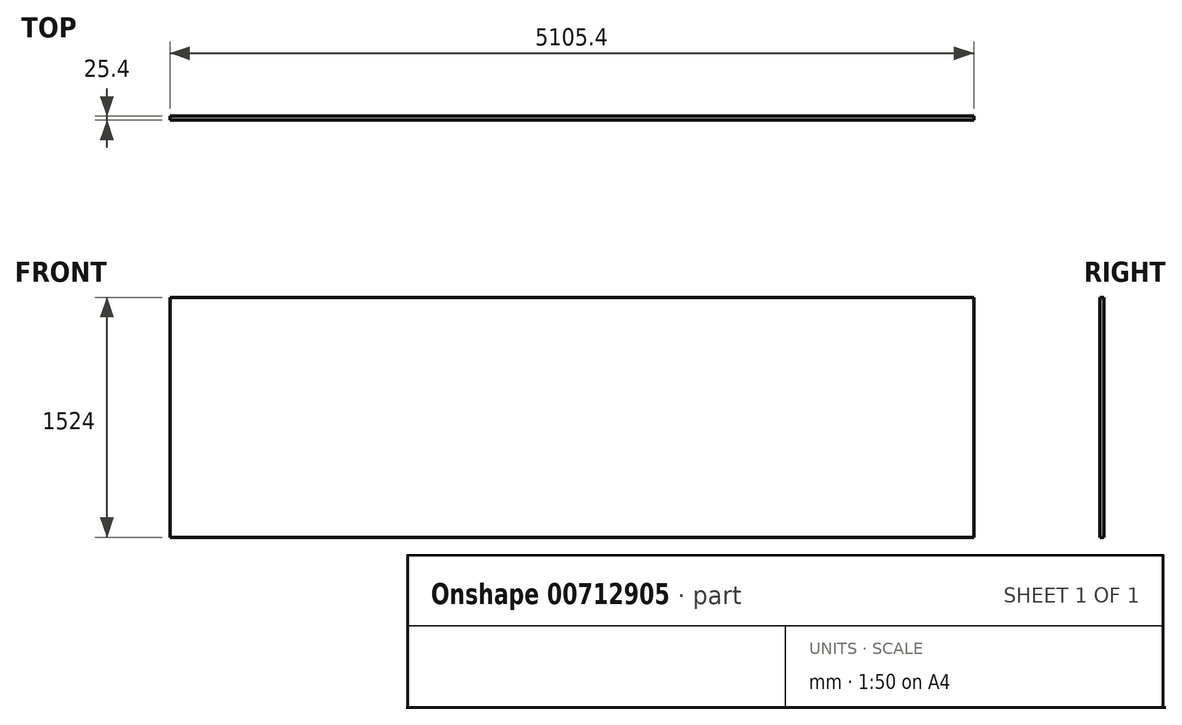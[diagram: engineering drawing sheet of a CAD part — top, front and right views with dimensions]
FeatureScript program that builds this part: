
annotation { "Feature Type Name" : "Feature", "Feature Type Description" : "" }
export const myFeature = defineFeature(function(context is Context, id is Id, definition is map)
    precondition{}
    {
        {
            var Q0;
            Q0=qCreatedBy(makeId("Front.planeOp"),FACE);
            var sketch = newSketch(context, id + "F0", { "sketchPlane" : qUnion([Q0])});
            skLineSegment(sketch, "E0.bottom", {"start": v(-2437.72, 1524) * mm, "end": v(2642.28, 1524) * mm});
            skLineSegment(sketch, "E0.top", {"start": v(-2437.72, 0) * mm, "end": v(2642.28, 0) * mm});
            skLineSegment(sketch, "E0.left", {"start": v(-2437.72, 1524) * mm, "end": v(-2437.72, 0) * mm});
            skLineSegment(sketch, "E0.right", {"start": v(2642.28, 1524) * mm, "end": v(2642.28, 0) * mm});
            skSolve(sketch);
        }
        {
            var Q0;
            Q0 = qSketchRegion(id + "F0", true);
            extrude(context, id + "F1", {"entities" : qUnion([Q0]), "oppositeDirection" : true, "depth" : 25.4 * mm, "offsetDistance" : 25.4 * mm});
        }
        {
            var Q0;
            Q0=makeQuery(id+"F1.opExtrude","SWEPT_FACE",FACE,{"disambiguationData":[OSD([sQuery(id+"F0.wireOp",EDGE,"E0.right")])]});
            extrude(context, id + "F2", {"entities" : qUnion([Q0]), "operationType" : NewBodyOperationType.ADD, "depth" : 25.4 * mm, "offsetDistance" : 25.4 * mm});
        }
    });
